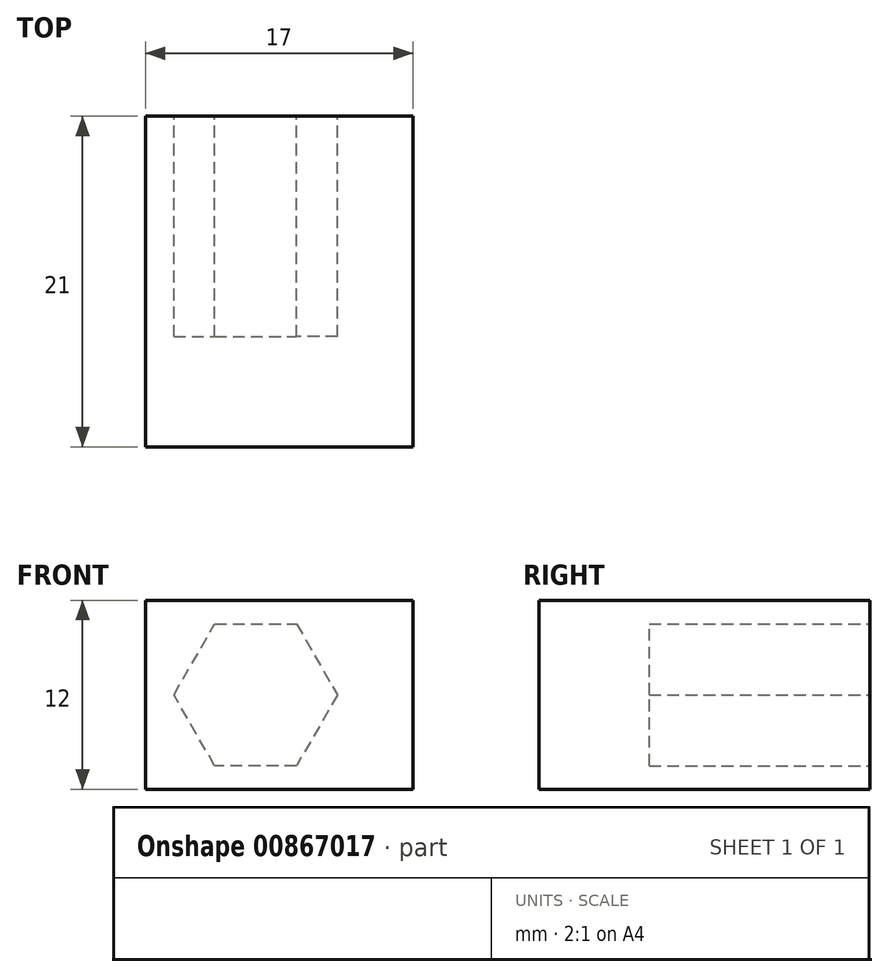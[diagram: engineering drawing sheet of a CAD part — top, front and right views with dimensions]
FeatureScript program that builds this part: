
annotation { "Feature Type Name" : "Feature", "Feature Type Description" : "" }
export const myFeature = defineFeature(function(context is Context, id is Id, definition is map)
    precondition{}
    {
        {
            var Q0;
            Q0=qCreatedBy(makeId("Front.planeOp"),FACE);
            var sketch = newSketch(context, id + "F0", { "sketchPlane" : qUnion([Q0])});
            skCircle(sketch, "E0.cCircle", {"center": v(0, 0) * mm, "radius": 4.5 * mm, "construction": true});
            skLineSegment(sketch, "E0.0", {"start": v(-2.6, 4.5) * mm, "end": v(2.6, 4.5) * mm});
            skLineSegment(sketch, "E0.1", {"start": v(2.6, 4.5) * mm, "end": v(5.2, 0) * mm});
            skLineSegment(sketch, "E0.2", {"start": v(5.2, 0) * mm, "end": v(2.6, -4.5) * mm});
            skLineSegment(sketch, "E0.3", {"start": v(2.6, -4.5) * mm, "end": v(-2.6, -4.5) * mm});
            skLineSegment(sketch, "E0.4", {"start": v(-2.6, -4.5) * mm, "end": v(-5.2, 0) * mm});
            skLineSegment(sketch, "E0.5", {"start": v(-5.2, 0) * mm, "end": v(-2.6, 4.5) * mm});
            skPoint(sketch, "E0.0.midPoint", {"position": v(0, 4.5) * mm});
            skLineSegment(sketch, "E1.bottom", {"start": v(10, 6) * mm, "end": v(-7, 6) * mm});
            skLineSegment(sketch, "E1.top", {"start": v(10, -6) * mm, "end": v(-7, -6) * mm});
            skLineSegment(sketch, "E1.left", {"start": v(10, 6) * mm, "end": v(10, -6) * mm});
            skLineSegment(sketch, "E1.right", {"start": v(-7, 6) * mm, "end": v(-7, -6) * mm});
            skLineSegment(sketch, "E2", {"start": v(-7, 0) * mm, "end": v(10, 0) * mm, "construction": true});
            skLineSegment(sketch, "E3", {"start": v(1.5, 6) * mm, "end": v(1.5, -6) * mm, "construction": true});
            skSolve(sketch);
        }
        {
            var Q0;
            Q0 = qSketchRegion(id + "F0", true);
            var Q1;
            Q1=makeQuery(id+"F0.imprint","IMPRINT",FACE,{"disambiguationData":[TD([[makeQuery(id+"F0.imprint","IMPRINT",EDGE,{"derivedFrom":sQuery(id+"F0.wireOp",EDGE,"E0.0")}),-1.0]])]});
            extrude(context, id + "F1", {"entities" : qUnion([Q0, Q1]), "depth" : 21 * mm, "offsetDistance" : 25 * mm});
        }
        {
            var Q0;
            Q0=makeQuery(id+"F0.imprint","IMPRINT",FACE,{"disambiguationData":[TD([[makeQuery(id+"F0.imprint","IMPRINT",EDGE,{"derivedFrom":sQuery(id+"F0.wireOp",EDGE,"E0.0")}),-1.0]])]});
            extrude(context, id + "F2", {"entities" : qUnion([Q0]), "operationType" : NewBodyOperationType.REMOVE, "depth" : 14 * mm, "offsetDistance" : 25 * mm});
        }
    });
